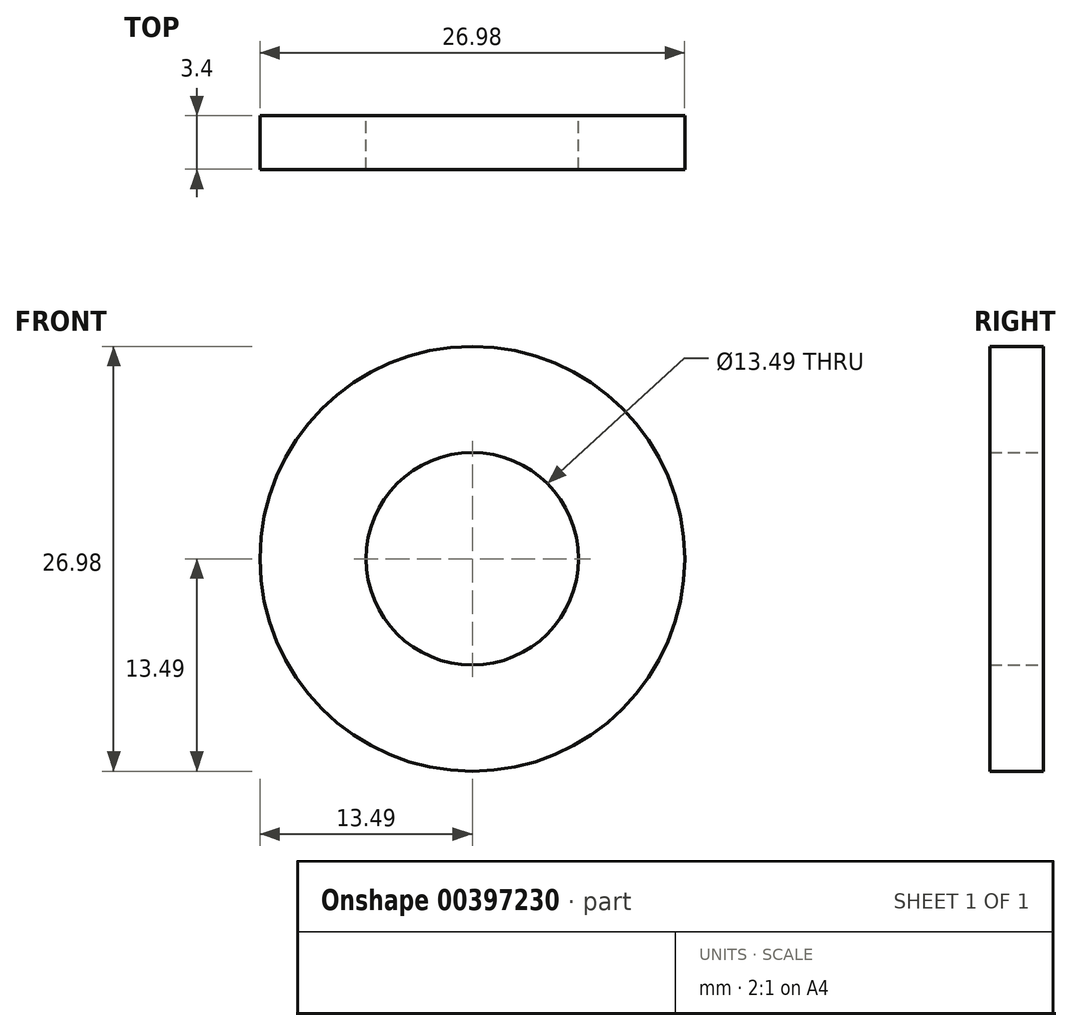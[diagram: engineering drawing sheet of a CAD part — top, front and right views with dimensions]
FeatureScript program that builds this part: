
annotation { "Feature Type Name" : "Feature", "Feature Type Description" : "" }
export const myFeature = defineFeature(function(context is Context, id is Id, definition is map)
    precondition{}
    {
        {
            var Q0;
            Q0=qCreatedBy(makeId("Front.planeOp"),FACE);
            var sketch = newSketch(context, id + "F0", { "sketchPlane" : qUnion([Q0])});
            skCircle(sketch, "E0", {"center": v(0, 0) * mm, "radius": 13.5 * mm});
            skCircle(sketch, "E1", {"center": v(0, 0) * mm, "radius": 6.75 * mm});
            skSolve(sketch);
        }
        {
            var Q0;
            Q0=qSketchRegion(id+"F0",true);
            extrude(context, id + "F1", {"entities" : qUnion([Q0]), "depth" : 3.4 * mm});
        }
    });
